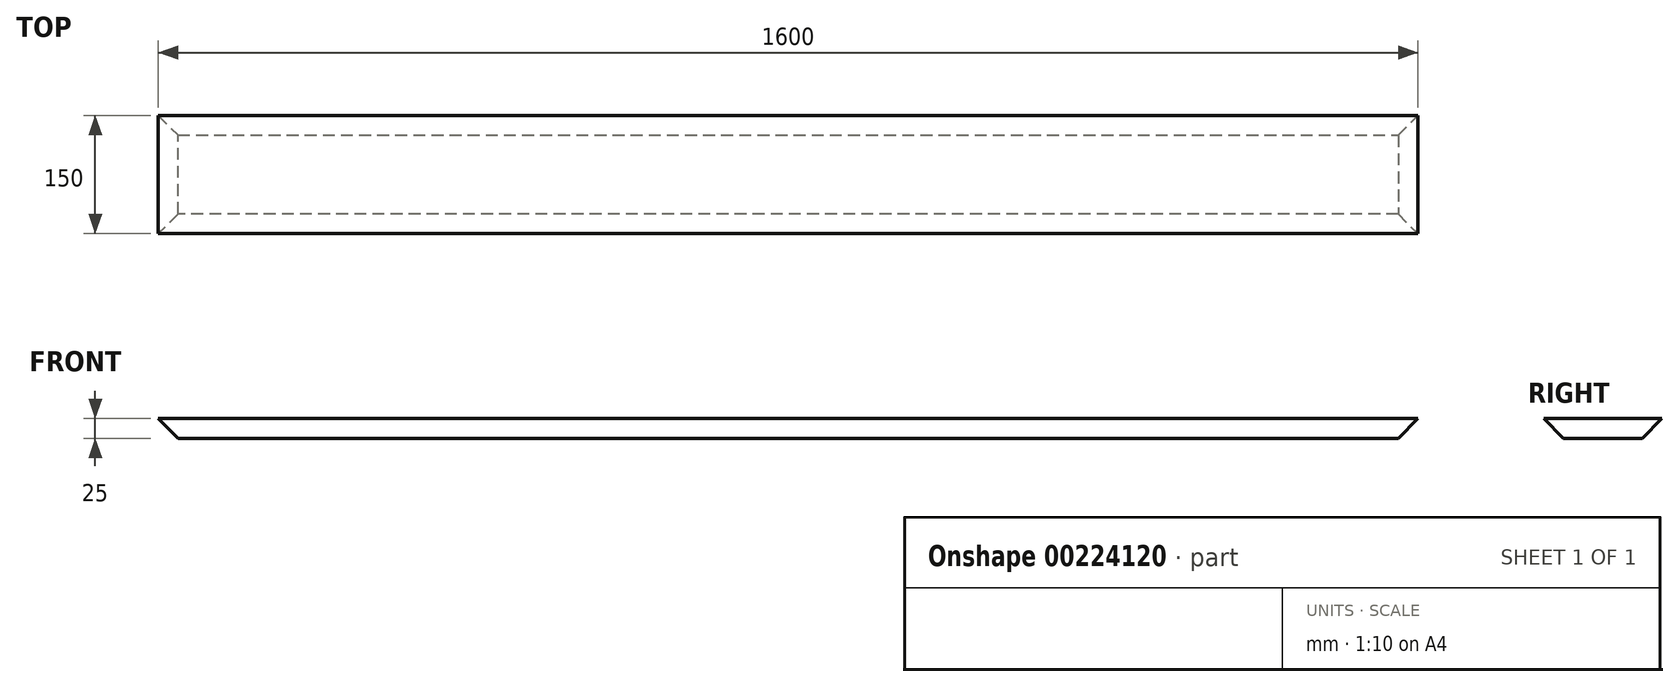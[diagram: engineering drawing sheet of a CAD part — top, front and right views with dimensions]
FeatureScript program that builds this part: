
annotation { "Feature Type Name" : "Feature", "Feature Type Description" : "" }
export const myFeature = defineFeature(function(context is Context, id is Id, definition is map)
    precondition{}
    {
        {
            var Q0;
            Q0=qCreatedBy(makeId("Top.planeOp"),FACE);
            var sketch = newSketch(context, id + "F0", { "sketchPlane" : qUnion([Q0])});
            skLineSegment(sketch, "E0.bottom", {"start": v(-800, 75) * mm, "end": v(800, 75) * mm});
            skLineSegment(sketch, "E0.top", {"start": v(-800, -75) * mm, "end": v(800, -75) * mm});
            skLineSegment(sketch, "E0.left", {"start": v(-800, 75) * mm, "end": v(-800, -75) * mm});
            skLineSegment(sketch, "E0.right", {"start": v(800, 75) * mm, "end": v(800, -75) * mm});
            skLineSegment(sketch, "E1", {"start": v(0, 75) * mm, "end": v(0, -75) * mm, "construction": true});
            skLineSegment(sketch, "E2", {"start": v(-800, 0) * mm, "end": v(800, 0) * mm, "construction": true});
            skSolve(sketch);
        }
        {
            var Q0;
            Q0=makeQuery(id+"F0.imprint","IMPRINT",FACE,{"disambiguationData":[TD([[makeQuery(id+"F0.imprint","IMPRINT",EDGE,{"derivedFrom":sQuery(id+"F0.wireOp",EDGE,"E0.bottom")}),-1.0]])]});
            extrude(context, id + "F1", {"entities" : qUnion([Q0]), "endBound" : BoundingType.SYMMETRIC, "depth" : 25 * mm});
        }
        {
            var Q0;
            Q0=makeQuery(id+"F1.opExtrude","CAP_EDGE",EDGE,{"disambiguationData":[OSD([sQuery(id+"F0.wireOp",EDGE,"E0.bottom")])],"isStart":true});
            var Q1;
            Q1=makeQuery(id+"F1.opExtrude","CAP_EDGE",EDGE,{"disambiguationData":[OSD([sQuery(id+"F0.wireOp",EDGE,"E0.left")])],"isStart":true});
            var Q2;
            Q2=makeQuery(id+"F1.opExtrude","CAP_EDGE",EDGE,{"disambiguationData":[OSD([sQuery(id+"F0.wireOp",EDGE,"E0.top")])],"isStart":true});
            var Q3;
            Q3=makeQuery(id+"F1.opExtrude","CAP_EDGE",EDGE,{"disambiguationData":[OSD([sQuery(id+"F0.wireOp",EDGE,"E0.right")])],"isStart":true});
            chamfer(context, id + "F2", {"entities" : qUnion([Q0, Q1, Q2, Q3]), "width" : 25 * mm, "tangentPropagation" : true});
        }
    });
